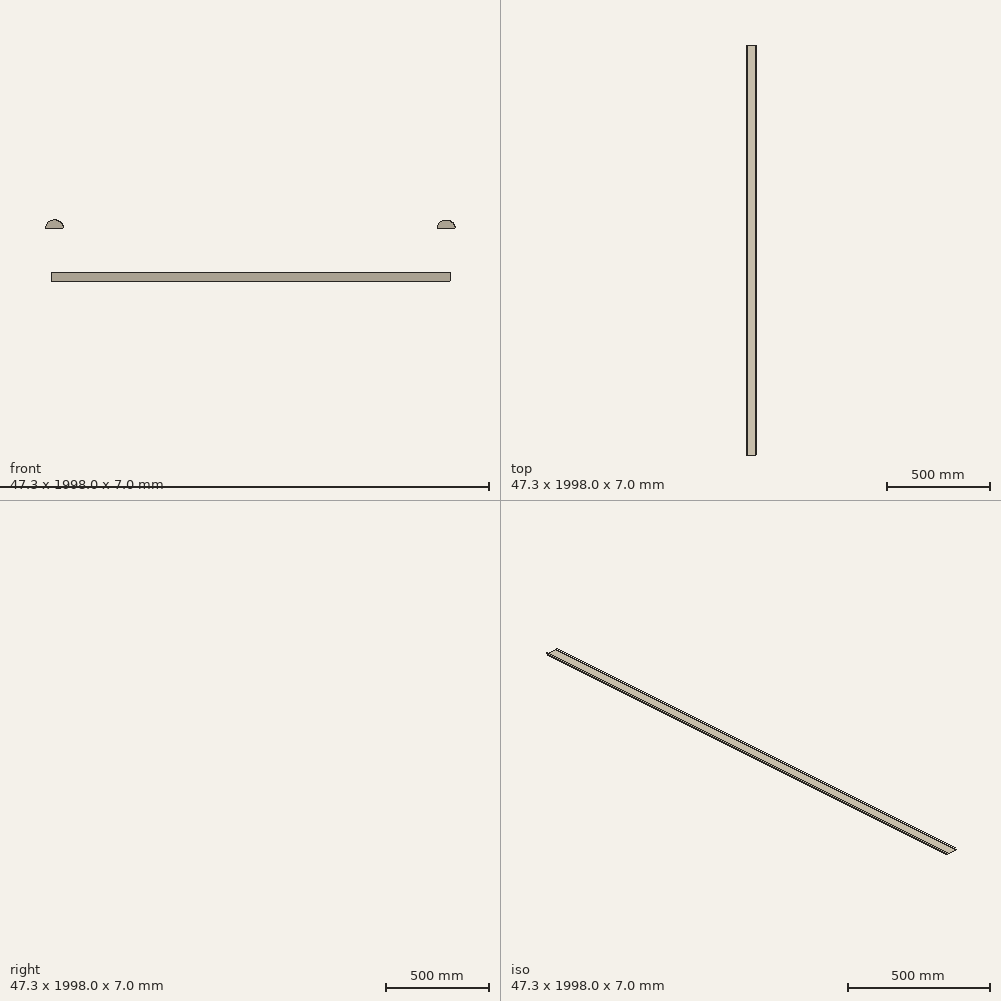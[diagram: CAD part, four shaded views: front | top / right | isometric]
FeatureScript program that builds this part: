
annotation { "Feature Type Name" : "Feature", "Feature Type Description" : "" }
export const myFeature = defineFeature(function(context is Context, id is Id, definition is map)
    precondition{}
    {
        {
            var Q0;
            Q0=qCreatedBy(makeId("Front.planeOp"),FACE);
            var sketch = newSketch(context, id + "F0", { "sketchPlane" : qUnion([Q0])});
            skLineSegment(sketch, "E0.bottom", {"start": v(-23.05, 0.5) * mm, "end": v(23.05, 0.5) * mm});
            skLineSegment(sketch, "E0.top", {"start": v(-23.05, -0.5) * mm, "end": v(23.05, -0.5) * mm});
            skLineSegment(sketch, "E0.left", {"start": v(-23.05, 0.5) * mm, "end": v(-23.05, -0.5) * mm});
            skLineSegment(sketch, "E0.right", {"start": v(23.05, 0.5) * mm, "end": v(23.05, -0.5) * mm});
            skPoint(sketch, "E0.middle", {"position": v(0, 0) * mm});
            skLineSegment(sketch, "E1.bottom", {"start": v(-23.05, 0.5) * mm, "end": v(-22.05, 0.5) * mm});
            skLineSegment(sketch, "E1.top", {"start": v(-23.05, 5.5) * mm, "end": v(-22.05, 5.5) * mm});
            skLineSegment(sketch, "E1.left", {"start": v(-23.05, 0.5) * mm, "end": v(-23.05, 5.5) * mm});
            skLineSegment(sketch, "E1.right", {"start": v(-22.05, 0.5) * mm, "end": v(-22.05, 5.5) * mm});
            skLineSegment(sketch, "E2.bottom", {"start": v(23.05, 0.5) * mm, "end": v(22.05, 0.5) * mm});
            skLineSegment(sketch, "E2.top", {"start": v(23.05, 5.5) * mm, "end": v(22.05, 5.5) * mm});
            skLineSegment(sketch, "E2.left", {"start": v(23.05, 0.5) * mm, "end": v(23.05, 5.5) * mm});
            skLineSegment(sketch, "E2.right", {"start": v(22.05, 0.5) * mm, "end": v(22.05, 5.5) * mm});
            skPoint(sketch, "E3.endSnap0", {"position": v(22.55, 5.5) * mm});
            skLineSegment(sketch, "E4", {"start": v(-23.7, 5.5) * mm, "end": v(-21.6, 5.5) * mm});
            skLineSegment(sketch, "E5", {"start": v(21.48, 5.5) * mm, "end": v(23.58, 5.5) * mm});
            skArc(sketch, "E6", {"start": v(-21.6, 5.5) * mm, "mid": v(-22.64, 6.55) * mm, "end": v(-23.7, 5.5) * mm});
            skArc(sketch, "E7", {"start": v(23.58, 5.5) * mm, "mid": v(22.53, 6.54) * mm, "end": v(21.48, 5.5) * mm});
            skSolve(sketch);
        }
        {
            var Q0;
            {var subQ2=sQuery(id+"F0.wireOp",EDGE,"E6");Q0=makeQuery(id+"F0.imprint","IMPRINT",FACE,{"disambiguationData":[TD([[makeQuery(id+"F0.imprint","IMPRINT",EDGE,{"derivedFrom":subQ2}),1.0]])]});}
            var Q1;
            Q1=makeQuery(id+"F0.imprint","IMPRINT",FACE,{"disambiguationData":[TD([[makeQuery(id+"F0.imprint","IMPRINT",EDGE,{"derivedFrom":sQuery(id+"F0.wireOp",EDGE,"E1.bottom")}),1.0]])]});
            var Q2;
            Q2=makeQuery(id+"F0.imprint","IMPRINT",FACE,{"disambiguationData":[TD([[makeQuery(id+"F0.imprint","IMPRINT",EDGE,{"derivedFrom":sQuery(id+"F0.wireOp",EDGE,"E0.bottom")}),-1.0]])]});
            var Q3;
            Q3=makeQuery(id+"F0.imprint","IMPRINT",FACE,{"disambiguationData":[TD([[makeQuery(id+"F0.imprint","IMPRINT",EDGE,{"derivedFrom":sQuery(id+"F0.wireOp",EDGE,"E2.bottom")}),-1.0]])]});
            var Q4;
            {var subQ2=sQuery(id+"F0.wireOp",EDGE,"E7");Q4=makeQuery(id+"F0.imprint","IMPRINT",FACE,{"disambiguationData":[TD([[makeQuery(id+"F0.imprint","IMPRINT",EDGE,{"derivedFrom":subQ2}),1.0]])]});}
            extrude(context, id + "F1", {"entities" : qUnion([Q0, Q1, Q2, Q3, Q4]), "endBound" : BoundingType.SYMMETRIC, "depth" : 1998 * mm, "offsetDistance" : 25 * mm});
        }
    });
